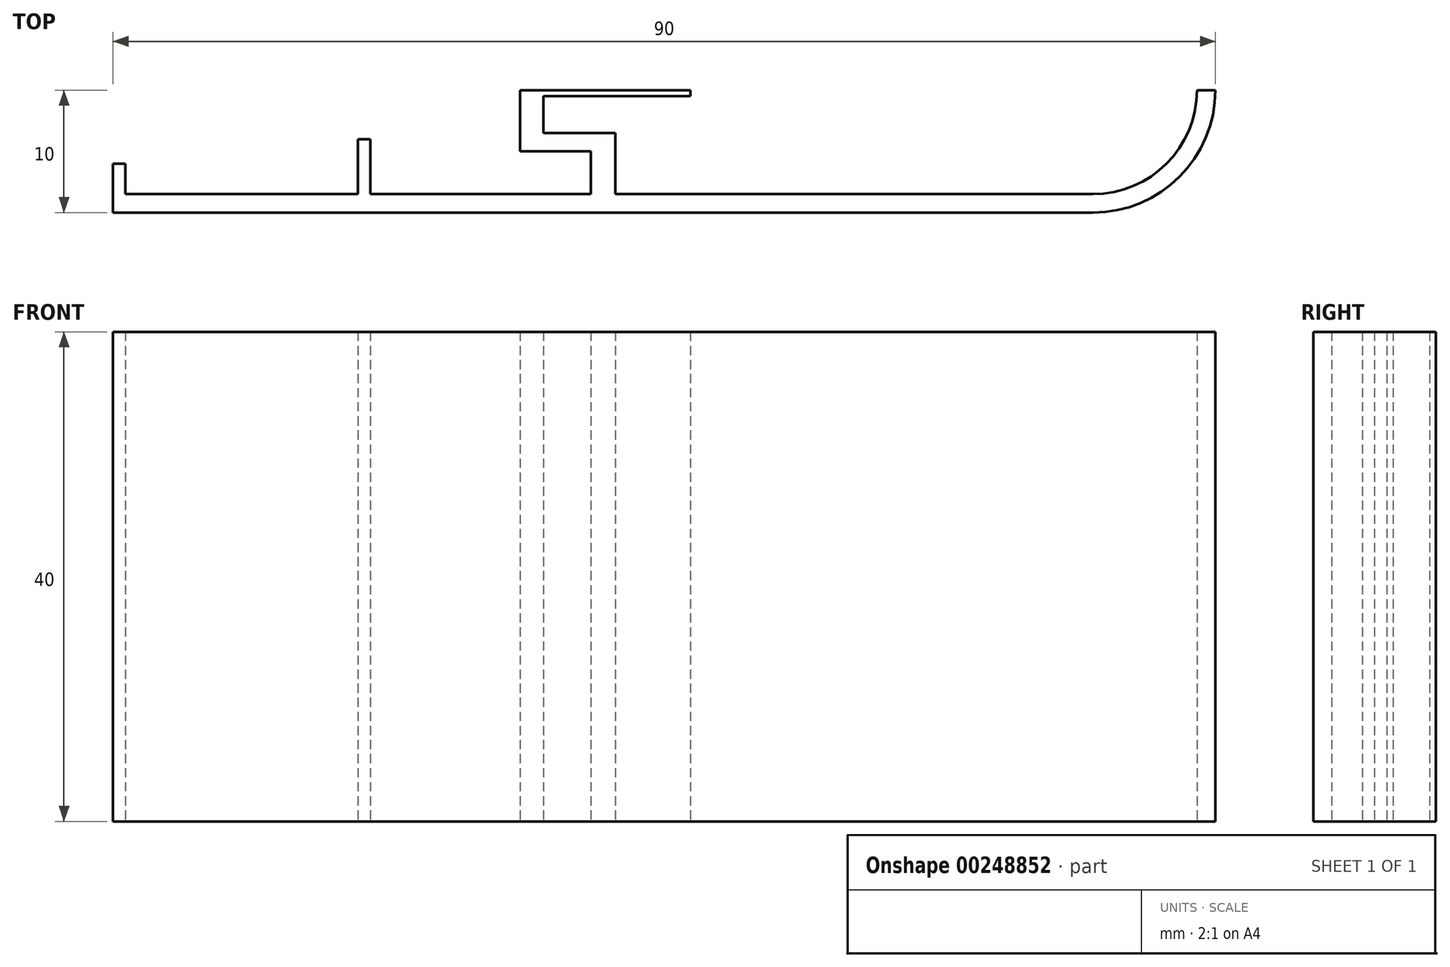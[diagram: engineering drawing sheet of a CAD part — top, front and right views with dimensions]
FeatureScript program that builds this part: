
annotation { "Feature Type Name" : "Feature", "Feature Type Description" : "" }
export const myFeature = defineFeature(function(context is Context, id is Id, definition is map)
    precondition{}
    {
        {
            var Q0;
            Q0=qCreatedBy(makeId("Top.planeOp"),FACE);
            var sketch = newSketch(context, id + "F0", { "sketchPlane" : qUnion([Q0])});
            skLineSegment(sketch, "E0", {"start": v(-0.9, -20) * mm, "end": v(-80, -20) * mm});
            skLineSegment(sketch, "E1", {"start": v(-0.9, 0) * mm, "end": v(-80, 0) * mm});
            skPoint(sketch, "E2.endSnap0", {"position": v(-40, -20) * mm});
            skLineSegment(sketch, "E3", {"start": v(-40.78, -1.5) * mm, "end": v(-59, -1.5) * mm});
            skLineSegment(sketch, "E4", {"start": v(-79, -1.5) * mm, "end": v(-60, -1.5) * mm});
            skLineSegment(sketch, "E5", {"start": v(-41, -18.5) * mm, "end": v(-59, -18.5) * mm});
            skLineSegment(sketch, "E6", {"start": v(-80, -18.5) * mm, "end": v(-80, -20) * mm});
            skLineSegment(sketch, "E7", {"start": v(-80, -1.5) * mm, "end": v(-80, 0) * mm});
            skLineSegment(sketch, "E8", {"start": v(-39, -18.5) * mm, "end": v(-6.21, -18.5) * mm});
            skPoint(sketch, "E9.start.orphan", {"position": v(-40, 0) * mm});
            skPoint(sketch, "E10.start.orphan", {"position": v(0, -10) * mm});
            skPoint(sketch, "E11.orphan", {"position": v(0, -1.5) * mm});
            skLineSegment(sketch, "E12", {"start": v(-60, -18.5) * mm, "end": v(-60, -14) * mm});
            skPoint(sketch, "E12.endSnap0", {"position": v(-60, -18.5) * mm});
            skLineSegment(sketch, "E13", {"start": v(-60, -1.5) * mm, "end": v(-60, -6) * mm});
            skLineSegment(sketch, "E14", {"start": v(-80, -18.5) * mm, "end": v(-80, -16) * mm});
            skLineSegment(sketch, "E15", {"start": v(-80, -1.5) * mm, "end": v(-80, -4) * mm});
            skLineSegment(sketch, "E16", {"start": v(-59, -18.5) * mm, "end": v(-59, -14) * mm});
            skLineSegment(sketch, "E17", {"start": v(-59, -1.5) * mm, "end": v(-59, -6) * mm});
            skLineSegment(sketch, "E18", {"start": v(-60, -14) * mm, "end": v(-59, -14) * mm});
            skLineSegment(sketch, "E19", {"start": v(-60, -6) * mm, "end": v(-59, -6) * mm});
            skLineSegment(sketch, "E20", {"start": v(-79, -18.5) * mm, "end": v(-79, -16) * mm});
            skLineSegment(sketch, "E21", {"start": v(-79, -1.5) * mm, "end": v(-79, -4) * mm});
            skLineSegment(sketch, "E22", {"start": v(-80, -4) * mm, "end": v(-79, -4) * mm});
            skLineSegment(sketch, "E23", {"start": v(-80, -16) * mm, "end": v(-79, -16) * mm});
            skLineSegment(sketch, "E24.trimOffspring", {"start": v(-60, -18.5) * mm, "end": v(-79, -18.5) * mm});
            skPoint(sketch, "E25.orphan", {"position": v(-40, -18.5) * mm});
            skLineSegment(sketch, "E26.trimOffspring", {"start": v(-59, -1.5) * mm, "end": v(-40.78, -1.5) * mm});
            skLineSegment(sketch, "E27.trimOffspring", {"start": v(-60, -1.5) * mm, "end": v(-79, -1.5) * mm});
            skLineSegment(sketch, "E28.trimOffspring", {"start": v(-38.85, -1.5) * mm, "end": v(-6.21, -1.5) * mm});
            skPoint(sketch, "E29.orphan", {"position": v(-40, -1.5) * mm});
            skLineSegment(sketch, "E30", {"start": v(-38.85, -1.5) * mm, "end": v(-38.85, -4.5) * mm});
            skLineSegment(sketch, "E31", {"start": v(-40.78, -1.5) * mm, "end": v(-40.78, -6) * mm});
            skLineSegment(sketch, "E32", {"start": v(-40.78, -6) * mm, "end": v(-34.78, -6) * mm});
            skLineSegment(sketch, "E33", {"start": v(-38.85, -4.5) * mm, "end": v(-32.85, -4.5) * mm});
            skLineSegment(sketch, "E34", {"start": v(-32.85, -4.5) * mm, "end": v(-32.85, -10.5) * mm});
            skLineSegment(sketch, "E35", {"start": v(-34.78, -6) * mm, "end": v(-34.78, -9) * mm});
            skLineSegment(sketch, "E36", {"start": v(-34.78, -9) * mm, "end": v(-46.78, -9) * mm});
            skLineSegment(sketch, "E37", {"start": v(-32.85, -10.5) * mm, "end": v(-44.85, -10.5) * mm});
            skLineSegment(sketch, "E38", {"start": v(-46.78, -9) * mm, "end": v(-46.78, -15) * mm});
            skLineSegment(sketch, "E39", {"start": v(-44.85, -10.5) * mm, "end": v(-44.85, -13.5) * mm});
            skLineSegment(sketch, "E40", {"start": v(-39, -18.5) * mm, "end": v(-39, -13.5) * mm});
            skLineSegment(sketch, "E41", {"start": v(-44.85, -13.5) * mm, "end": v(-39, -13.5) * mm});
            skLineSegment(sketch, "E42", {"start": v(-46.78, -15) * mm, "end": v(-41, -15) * mm});
            skLineSegment(sketch, "E43", {"start": v(-41, -15) * mm, "end": v(-41, -18.5) * mm});
            skPoint(sketch, "E44.orphan", {"position": v(-1.5, -1.5) * mm});
            skPoint(sketch, "E45.orphan", {"position": v(0, -20) * mm});
            skPoint(sketch, "E46.orphan", {"position": v(0, 0) * mm});
            skLineSegment(sketch, "E47", {"start": v(-0.9, 0) * mm, "end": v(0, 0) * mm});
            skLineSegment(sketch, "E48", {"start": v(-6.21, -1.5) * mm, "end": v(0, -1.5) * mm});
            skLineSegment(sketch, "E49", {"start": v(-0.9, -20) * mm, "end": v(0, -20) * mm});
            skLineSegment(sketch, "E50", {"start": v(-6.21, -18.5) * mm, "end": v(0, -18.5) * mm});
            skArc(sketch, "E51", {"start": v(0, -18.5) * mm, "mid": v(8.5, -10) * mm, "end": v(0, -1.5) * mm});
            skArc(sketch, "E52", {"start": v(0, -20) * mm, "mid": v(10, -10) * mm, "end": v(0, 0) * mm});
            skLineSegment(sketch, "E53", {"start": v(10, -10) * mm, "end": v(-80, -10) * mm});
            skLineSegment(sketch, "E54", {"start": v(-80, -4) * mm, "end": v(-80, -16) * mm});
            skSolve(sketch);
        }
        {
            var Q0;
            Q0=makeQuery(id+"F0.imprint","IMPRINT",FACE,{"disambiguationData":[TD([[makeQuery(id+"F0.imprint","IMPRINT",EDGE,{"derivedFrom":sQuery(id+"F0.wireOp",EDGE,"E0")}),-1.0]])]});
            extrude(context, id + "F1", {"entities" : qUnion([Q0]), "depth" : 40 * mm});
        }
    });
